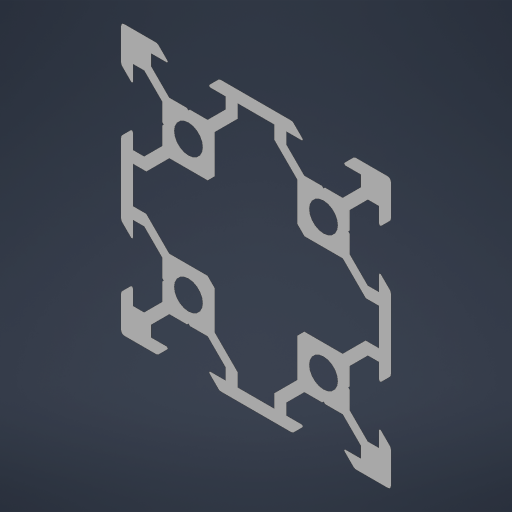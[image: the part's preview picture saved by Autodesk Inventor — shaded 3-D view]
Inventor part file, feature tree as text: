
AUTODESK INVENTOR PART (.ipt)
format: ipt  version: 2023.1 (Build 271208000, 208)  size: 670,720 bytes
history: native  units: mm
features: other x1, extrude x1, sketch x1, projected_geometry x1
ambient origin geometry x8: Origin, YZ Plane, XZ Plane, XY Plane, X Axis, Y Axis, Z Axis, Center Point
bodies: Solid2 (feature_tree), Solid1 (feature_tree), Body2 (feature_tree)
feature tree (4):
  other  "40x40-V-Slot-Extrusion.step"
  extrude  "Extrusion1"  [1 undecoded]
  sketch  "Sketch1"  dims[d1=0.0mm]
  projected_geometry  "Projected Loop1"
note: 1 required parameter value undecoded (feature->parameter linkage not recoverable at this tier; creation-order binding heuristic only, values carry confidence <= 0.55)
